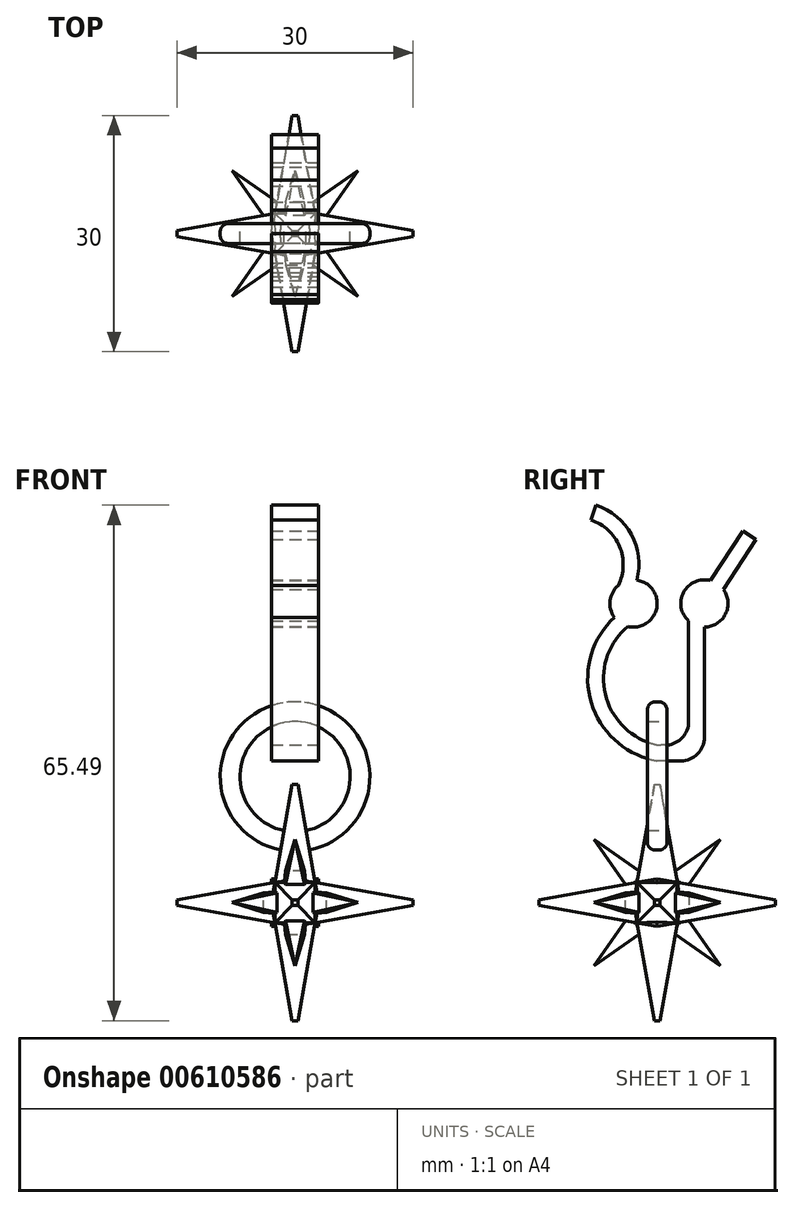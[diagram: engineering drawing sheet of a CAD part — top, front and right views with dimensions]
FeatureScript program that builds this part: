
annotation { "Feature Type Name" : "Feature", "Feature Type Description" : "" }
export const myFeature = defineFeature(function(context is Context, id is Id, definition is map)
    precondition{}
    {
        {
            var Q0;
            Q0=qCreatedBy(makeId("Front.planeOp"),FACE);
            var sketch = newSketch(context, id + "F0", { "sketchPlane" : qUnion([Q0])});
            skLineSegment(sketch, "E0.bottom", {"start": v(-3, 3) * mm, "end": v(3, 3) * mm});
            skLineSegment(sketch, "E0.top", {"start": v(-3, -3) * mm, "end": v(3, -3) * mm});
            skLineSegment(sketch, "E0.left", {"start": v(-3, 3) * mm, "end": v(-3, -3) * mm});
            skLineSegment(sketch, "E0.right", {"start": v(3, 3) * mm, "end": v(3, -3) * mm});
            skLineSegment(sketch, "E1", {"start": v(0, 3) * mm, "end": v(0, -47.6) * mm, "construction": true});
            skLineSegment(sketch, "E2", {"start": v(3, 0) * mm, "end": v(-3, 0) * mm, "construction": true});
            skPoint(sketch, "E3", {"position": v(0, 0) * mm});
            skPoint(sketch, "E4.orphan", {"position": v(0, -3) * mm});
            skCircle(sketch, "E5", {"center": v(0, 16) * mm, "radius": 7 * mm});
            skCircle(sketch, "E6", {"center": v(0, 16) * mm, "radius": 9.5 * mm});
            skSolve(sketch);
        }
        {
            var Q0;
            Q0=makeQuery(id+"F0.imprint","IMPRINT",FACE,{"disambiguationData":[TD([[makeQuery(id+"F0.imprint","IMPRINT",EDGE,{"derivedFrom":sQuery(id+"F0.wireOp",EDGE,"E0.bottom")}),-1.0]])]});
            extrude(context, id + "F1", {"entities" : qUnion([Q0]), "depth" : 15 * mm, "offsetDistance" : 25 * mm, "hasDraft" : true, "draftAngle" : 10 * degree, "draftPullDirection" : true, "hasSecondDirection" : true, "secondDirectionOppositeDirection" : true, "secondDirectionDepth" : 15 * mm, "hasSecondDirectionDraft" : true, "secondDirectionDraftAngle" : 10 * degree, "secondDirectionDraftPullDirection" : true});
        }
        {
            var Q0;
            Q0=qCreatedBy(makeId("Top.planeOp"),FACE);
            var sketch = newSketch(context, id + "F2", { "sketchPlane" : qUnion([Q0])});
            skLineSegment(sketch, "E7.bottom", {"start": v(-3, -3) * mm, "end": v(3, -3) * mm});
            skLineSegment(sketch, "E7.top", {"start": v(-3, 3) * mm, "end": v(3, 3) * mm});
            skLineSegment(sketch, "E7.left", {"start": v(3, -3) * mm, "end": v(3, 3) * mm});
            skLineSegment(sketch, "E7.right", {"start": v(-3, -3) * mm, "end": v(-3, 3) * mm});
            skLineSegment(sketch, "E8", {"start": v(-3, 0) * mm, "end": v(3, 0) * mm, "construction": true});
            skLineSegment(sketch, "E9", {"start": v(0, -3) * mm, "end": v(0, 3) * mm, "construction": true});
            skPoint(sketch, "E10", {"position": v(0, 0) * mm});
            skSolve(sketch);
        }
        {
            var Q0;
            Q0 = qSketchRegion(id + "F2", true);
            extrude(context, id + "F3", {"entities" : qUnion([Q0]), "operationType" : NewBodyOperationType.ADD, "depth" : 15 * mm, "offsetDistance" : 25 * mm, "hasDraft" : true, "draftAngle" : 10 * degree, "draftPullDirection" : true, "hasSecondDirection" : true, "secondDirectionOppositeDirection" : true, "secondDirectionDepth" : 15 * mm, "hasSecondDirectionDraft" : true, "secondDirectionDraftAngle" : 10 * degree, "secondDirectionDraftPullDirection" : true});
        }
        {
            var Q0;
            Q0=qCreatedBy(makeId("Right.planeOp"),FACE);
            var sketch = newSketch(context, id + "F4", { "sketchPlane" : qUnion([Q0])});
            skLineSegment(sketch, "E11.bottom", {"start": v(-3, -3) * mm, "end": v(3, -3) * mm});
            skLineSegment(sketch, "E11.top", {"start": v(-3, 3) * mm, "end": v(3, 3) * mm});
            skLineSegment(sketch, "E11.left", {"start": v(-3, -3) * mm, "end": v(-3, 3) * mm});
            skLineSegment(sketch, "E11.right", {"start": v(3, -3) * mm, "end": v(3, 3) * mm});
            skLineSegment(sketch, "E12", {"start": v(-3, 0) * mm, "end": v(3, 0) * mm, "construction": true});
            skLineSegment(sketch, "E13", {"start": v(0, -3) * mm, "end": v(0, 3) * mm, "construction": true});
            skPoint(sketch, "E14", {"position": v(0, 0) * mm});
            skSolve(sketch);
        }
        {
            var Q0;
            Q0 = qSketchRegion(id + "F4", true);
            extrude(context, id + "F5", {"entities" : qUnion([Q0]), "operationType" : NewBodyOperationType.ADD, "depth" : 15 * mm, "offsetDistance" : 25 * mm, "hasDraft" : true, "draftAngle" : 10 * degree, "draftPullDirection" : true, "hasSecondDirection" : true, "secondDirectionOppositeDirection" : true, "secondDirectionDepth" : 15 * mm, "hasSecondDirectionDraft" : true, "secondDirectionDraftAngle" : 10 * degree, "secondDirectionDraftPullDirection" : true});
        }
        {
            var Q0;
            Q0=sQuery(id+"F0.wireOp",EDGE,"E1");
            var Q1;
            Q1=qCreatedBy(makeId("Front.planeOp"),FACE);
            cPlane(context, id + "F6", {"entities" : qUnion([Q0, Q1]), "cplaneType" : CPlaneType.LINE_ANGLE, "offset" : 25 * mm, "angle" : 45 * degree, "width" : 150 * mm, "height" : 150 * mm});
        }
        {
            var Q0;
            Q0=qCreatedBy(id+"F6.planeOp",FACE);
            var sketch = newSketch(context, id + "F7", { "sketchPlane" : qUnion([Q0])});
            skLineSegment(sketch, "E15.bottom", {"start": v(-2, 2) * mm, "end": v(2, 2) * mm});
            skLineSegment(sketch, "E15.top", {"start": v(-2, -2) * mm, "end": v(2, -2) * mm});
            skLineSegment(sketch, "E15.left", {"start": v(-2, 2) * mm, "end": v(-2, -2) * mm});
            skLineSegment(sketch, "E15.right", {"start": v(2, 2) * mm, "end": v(2, -2) * mm});
            skLineSegment(sketch, "E16", {"start": v(0, 2) * mm, "end": v(0, -2) * mm, "construction": true});
            skLineSegment(sketch, "E17", {"start": v(-2, 0) * mm, "end": v(2, 0) * mm, "construction": true});
            skPoint(sketch, "E18", {"position": v(0, 0) * mm});
            skSolve(sketch);
        }
        {
            var Q0;
            Q0 = qSketchRegion(id + "F7", true);
            extrude(context, id + "F8", {"entities" : qUnion([Q0]), "operationType" : NewBodyOperationType.ADD, "depth" : 12 * mm, "offsetDistance" : 25 * mm, "hasDraft" : true, "draftAngle" : 10 * degree, "draftPullDirection" : true, "hasSecondDirection" : true, "secondDirectionOppositeDirection" : true, "secondDirectionDepth" : 12 * mm, "hasSecondDirectionDraft" : true, "secondDirectionDraftAngle" : 10 * degree, "secondDirectionDraftPullDirection" : true});
        }
        {
            var Q0;
            Q0=sQuery(id+"F0.wireOp",EDGE,"E1");
            var Q1;
            Q1=qCreatedBy(id+"F6.planeOp",FACE);
            cPlane(context, id + "F9", {"entities" : qUnion([Q0, Q1]), "cplaneType" : CPlaneType.LINE_ANGLE, "offset" : 25 * mm, "angle" : 90 * degree, "width" : 150 * mm, "height" : 150 * mm});
        }
        {
            var Q0;
            Q0=qCreatedBy(id+"F9.planeOp",FACE);
            var sketch = newSketch(context, id + "F10", { "sketchPlane" : qUnion([Q0])});
            skLineSegment(sketch, "E19.bottom", {"start": v(-2, -2) * mm, "end": v(2, -2) * mm});
            skLineSegment(sketch, "E19.top", {"start": v(-2, 2) * mm, "end": v(2, 2) * mm});
            skLineSegment(sketch, "E19.left", {"start": v(-2, -2) * mm, "end": v(-2, 2) * mm});
            skLineSegment(sketch, "E19.right", {"start": v(2, -2) * mm, "end": v(2, 2) * mm});
            skLineSegment(sketch, "E20", {"start": v(-2, 0) * mm, "end": v(2, 0) * mm, "construction": true});
            skLineSegment(sketch, "E21", {"start": v(0, 2) * mm, "end": v(0, -2) * mm, "construction": true});
            skPoint(sketch, "E22", {"position": v(0, 0) * mm});
            skLineSegment(sketch, "E23", {"start": v(2, 2) * mm, "end": v(-19.37, -19.37) * mm, "construction": true});
            skSolve(sketch);
        }
        {
            var Q0;
            Q0 = qSketchRegion(id + "F10", true);
            extrude(context, id + "F11", {"entities" : qUnion([Q0]), "operationType" : NewBodyOperationType.ADD, "depth" : 12 * mm, "offsetDistance" : 25 * mm, "hasDraft" : true, "draftAngle" : 10 * degree, "draftPullDirection" : true, "hasSecondDirection" : true, "secondDirectionOppositeDirection" : true, "secondDirectionDepth" : 12 * mm, "hasSecondDirectionDraft" : true, "secondDirectionDraftAngle" : 10 * degree, "secondDirectionDraftPullDirection" : true});
        }
        {
            var Q0;
            Q0=qCreatedBy(makeId("Front.planeOp"),FACE);
            var sketch = newSketch(context, id + "F12", { "sketchPlane" : qUnion([Q0])});
            skLineSegment(sketch, "E24", {"start": v(89.66, 0) * mm, "end": v(-54.6, 0) * mm, "construction": true});
            skSolve(sketch);
        }
        {
            var Q0;
            Q0=qCreatedBy(makeId("Top.planeOp"),FACE);
            var Q1;
            Q1=sQuery(id+"F12.wireOp",EDGE,"E24");
            cPlane(context, id + "F13", {"entities" : qUnion([Q0, Q1]), "cplaneType" : CPlaneType.LINE_ANGLE, "offset" : 25 * mm, "angle" : 45 * degree, "width" : 150 * mm, "height" : 150 * mm});
        }
        {
            var Q0;
            Q0=qCreatedBy(id+"F13.planeOp",FACE);
            var sketch = newSketch(context, id + "F14", { "sketchPlane" : qUnion([Q0])});
            skLineSegment(sketch, "E25.bottom", {"start": v(-2, 2) * mm, "end": v(2, 2) * mm});
            skLineSegment(sketch, "E25.top", {"start": v(-2, -2) * mm, "end": v(2, -2) * mm});
            skLineSegment(sketch, "E25.left", {"start": v(-2, 2) * mm, "end": v(-2, -2) * mm});
            skLineSegment(sketch, "E25.right", {"start": v(2, 2) * mm, "end": v(2, -2) * mm});
            skLineSegment(sketch, "E26", {"start": v(-2, 0) * mm, "end": v(2, 0) * mm, "construction": true});
            skLineSegment(sketch, "E27", {"start": v(0, -2) * mm, "end": v(0, 2) * mm, "construction": true});
            skPoint(sketch, "E28", {"position": v(0, 0) * mm});
            skSolve(sketch);
        }
        {
            var Q0;
            Q0 = qSketchRegion(id + "F14", true);
            extrude(context, id + "F15", {"entities" : qUnion([Q0]), "operationType" : NewBodyOperationType.ADD, "depth" : 12 * mm, "offsetDistance" : 25 * mm, "hasDraft" : true, "draftAngle" : 10 * degree, "draftPullDirection" : true, "hasSecondDirection" : true, "secondDirectionOppositeDirection" : true, "secondDirectionDepth" : 12 * mm, "hasSecondDirectionDraft" : true, "secondDirectionDraftAngle" : 10 * degree, "secondDirectionDraftPullDirection" : true});
        }
        {
            var Q0;
            Q0=sQuery(id+"F12.wireOp",EDGE,"E24");
            var Q1;
            Q1=qCreatedBy(makeId("Top.planeOp"),FACE);
            cPlane(context, id + "F16", {"entities" : qUnion([Q0, Q1]), "cplaneType" : CPlaneType.LINE_ANGLE, "offset" : 25 * mm, "angle" : 45 * degree, "oppositeDirection" : true, "width" : 150 * mm, "height" : 150 * mm});
        }
        {
            var Q0;
            Q0=qCreatedBy(id+"F16.planeOp",FACE);
            var sketch = newSketch(context, id + "F17", { "sketchPlane" : qUnion([Q0])});
            skLineSegment(sketch, "E29.bottom", {"start": v(2, 2) * mm, "end": v(-2, 2) * mm});
            skLineSegment(sketch, "E29.top", {"start": v(2, -2) * mm, "end": v(-2, -2) * mm});
            skLineSegment(sketch, "E29.left", {"start": v(2, 2) * mm, "end": v(2, -2) * mm});
            skLineSegment(sketch, "E29.right", {"start": v(-2, 2) * mm, "end": v(-2, -2) * mm});
            skLineSegment(sketch, "E30", {"start": v(0, 2) * mm, "end": v(0, -2) * mm, "construction": true});
            skLineSegment(sketch, "E31", {"start": v(-2, 0) * mm, "end": v(2, 0) * mm, "construction": true});
            skPoint(sketch, "E32", {"position": v(0, 0) * mm});
            skSolve(sketch);
        }
        {
            var Q0;
            Q0 = qSketchRegion(id + "F17", true);
            extrude(context, id + "F18", {"entities" : qUnion([Q0]), "operationType" : NewBodyOperationType.ADD, "depth" : 12 * mm, "offsetDistance" : 25 * mm, "hasDraft" : true, "draftAngle" : 10 * degree, "draftPullDirection" : true, "hasSecondDirection" : true, "secondDirectionOppositeDirection" : true, "secondDirectionDepth" : 12 * mm, "hasSecondDirectionDraft" : true, "secondDirectionDraftAngle" : 10 * degree, "secondDirectionDraftPullDirection" : true});
        }
        {
            var Q0;
            Q0=makeQuery(id+"F0.imprint","IMPRINT",FACE,{"disambiguationData":[TD([[makeQuery(id+"F0.imprint","IMPRINT",EDGE,{"derivedFrom":sQuery(id+"F0.wireOp",EDGE,"E5")}),-1.0]])]});
            extrude(context, id + "F19", {"entities" : qUnion([Q0]), "operationType" : NewBodyOperationType.ADD, "depth" : 1.25 * mm, "offsetDistance" : 25 * mm, "hasSecondDirection" : true, "secondDirectionOppositeDirection" : true, "secondDirectionDepth" : 1.25 * mm});
        }
        {
            var Q0;
            Q0=makeQuery(id+"F19.opExtrude","CAP_EDGE",EDGE,{"disambiguationData":[OSD([sQuery(id+"F0.wireOp",EDGE,"E6")])],"isStart":false});
            var Q1;
            Q1=makeQuery(id+"F19.opExtrude","CAP_EDGE",EDGE,{"disambiguationData":[OSD([sQuery(id+"F0.wireOp",EDGE,"E6")])],"isStart":true});
            fillet(context, id + "F20", {"entities" : qUnion([Q0, Q1]), "radius" : 1 * mm, "tangentPropagation" : true, "allowEdgeOverflow" : false});
        }
        {
            var Q0;
            Q0=qCreatedBy(makeId("Right.planeOp"),FACE);
            var sketch = newSketch(context, id + "F21", { "sketchPlane" : qUnion([Q0])});
            skLineSegment(sketch, "E33.top", {"start": v(6, 18) * mm, "end": v(0, 18) * mm});
            skLineSegment(sketch, "E33.left", {"start": v(6, 38) * mm, "end": v(6, 18) * mm});
            skCircle(sketch, "E34", {"center": v(6, 38) * mm, "radius": 3 * mm});
            skLineSegment(sketch, "E35", {"start": v(4, 35.76) * mm, "end": v(4, 20) * mm});
            skLineSegment(sketch, "E36", {"start": v(4, 20) * mm, "end": v(0.18, 20) * mm});
            skPoint(sketch, "E37.orphan", {"position": v(0, 35.73) * mm});
            skLineSegment(sketch, "E38", {"start": v(6, 38) * mm, "end": v(-11.6, 38) * mm, "construction": true});
            skCircle(sketch, "E39", {"center": v(-3, 38) * mm, "radius": 3 * mm});
            skArc(sketch, "E40", {"start": v(-5.43, 36.24) * mm, "mid": v(-8.38, 25.43) * mm, "end": v(0, 18) * mm});
            skArc(sketch, "E41.0", {"start": v(-3.72, 35.09) * mm, "mid": v(-6.55, 26.3) * mm, "end": v(0.18, 20) * mm});
            skArc(sketch, "E42", {"start": v(-2.56, 40.97) * mm, "mid": v(-3.3, 46.75) * mm, "end": v(-7.76, 50.49) * mm});
            skArc(sketch, "E43.0", {"start": v(-4.93, 40.3) * mm, "mid": v(-4.78, 45.24) * mm, "end": v(-8.41, 48.6) * mm});
            skLineSegment(sketch, "E44", {"start": v(-8.41, 48.6) * mm, "end": v(-7.76, 50.49) * mm});
            skLineSegment(sketch, "E45", {"start": v(6.77, 40.9) * mm, "end": v(10.86, 47.2) * mm});
            skLineSegment(sketch, "E46", {"start": v(10.86, 47.2) * mm, "end": v(12.54, 46.12) * mm});
            skLineSegment(sketch, "E47", {"start": v(12.54, 46.12) * mm, "end": v(8.42, 39.77) * mm});
            skPoint(sketch, "E48.orphan", {"position": v(0, 20) * mm});
            skSolve(sketch);
        }
        {
            var Q0;
            {var subQ0=sQuery(id+"F21.wireOp",EDGE,"E45");Q0=makeQuery(id+"F21.imprint","IMPRINT",FACE,{"disambiguationData":[TD([[makeQuery(id+"F21.imprint","IMPRINT",EDGE,{"derivedFrom":subQ0}),-1.0]])]});}
            var Q1;
            {var subQ0=sQuery(id+"F21.wireOp",EDGE,"E34");var subQ1=makeQuery(id+"F21.imprint","INTERSECT",VERTEX,{"derivedFrom":[subQ0,sQuery(id+"F21.wireOp",EDGE,"E45")]});Q1=makeQuery(id+"F21.imprint","IMPRINT",FACE,{"disambiguationData":[TD([[makeQuery(id+"F21.imprint","IMPRINT",EDGE,{"disambiguationData":[TD([[subQ1,1.0]])],"derivedFrom":subQ0}),1.0]])]});}
            var Q2;
            {var subQ4=sQuery(id+"F21.wireOp",EDGE,"E33.top");Q2=makeQuery(id+"F21.imprint","IMPRINT",FACE,{"disambiguationData":[TD([[makeQuery(id+"F21.imprint","IMPRINT",EDGE,{"derivedFrom":subQ4}),-1.0]])]});}
            var Q3;
            {var subQ0=sQuery(id+"F21.wireOp",EDGE,"E39");var subQ1=makeQuery(id+"F21.imprint","INTERSECT",VERTEX,{"derivedFrom":[subQ0,sQuery(id+"F21.wireOp",EDGE,"E42")]});Q3=makeQuery(id+"F21.imprint","IMPRINT",FACE,{"disambiguationData":[TD([[makeQuery(id+"F21.imprint","IMPRINT",EDGE,{"disambiguationData":[TD([[subQ1,-1.0]])],"derivedFrom":subQ0}),1.0]])]});}
            var Q4;
            {var subQ0=sQuery(id+"F21.wireOp",EDGE,"E42");Q4=makeQuery(id+"F21.imprint","IMPRINT",FACE,{"disambiguationData":[TD([[makeQuery(id+"F21.imprint","IMPRINT",EDGE,{"derivedFrom":subQ0}),1.0]])]});}
            extrude(context, id + "F22", {"entities" : qUnion([Q0, Q1, Q2, Q3, Q4]), "oppositeDirection" : true, "depth" : 3 * mm, "offsetDistance" : 25 * mm, "hasSecondDirection" : true, "secondDirectionOppositeDirection" : false, "secondDirectionDepth" : 3 * mm});
        }
        {
            var Q0;
            Q0=makeQuery(id+"F22.opExtrude","SWEPT_EDGE",EDGE,{"disambiguationData":[OSD([sQuery(id+"F21.wireOp",EDGE,"E35"),sQuery(id+"F21.wireOp",EDGE,"E36")])]});
            var Q1;
            Q1=makeQuery(id+"F22.opExtrude","SWEPT_EDGE",EDGE,{"disambiguationData":[OSD([sQuery(id+"F21.wireOp",EDGE,"E33.top"),sQuery(id+"F21.wireOp",EDGE,"E33.left")])]});
            var Q2;
            Q2=makeQuery(id+"F22.opExtrude","SWEPT_EDGE",EDGE,{"disambiguationData":[OSD([sQuery(id+"F21.wireOp",EDGE,"E36"),sQuery(id+"F21.wireOp",EDGE,"E41.0")])]});
            fillet(context, id + "F23", {"entities" : qUnion([Q0, Q1, Q2]), "radius" : 3 * mm, "tangentPropagation" : true, "allowEdgeOverflow" : false});
        }
    });
